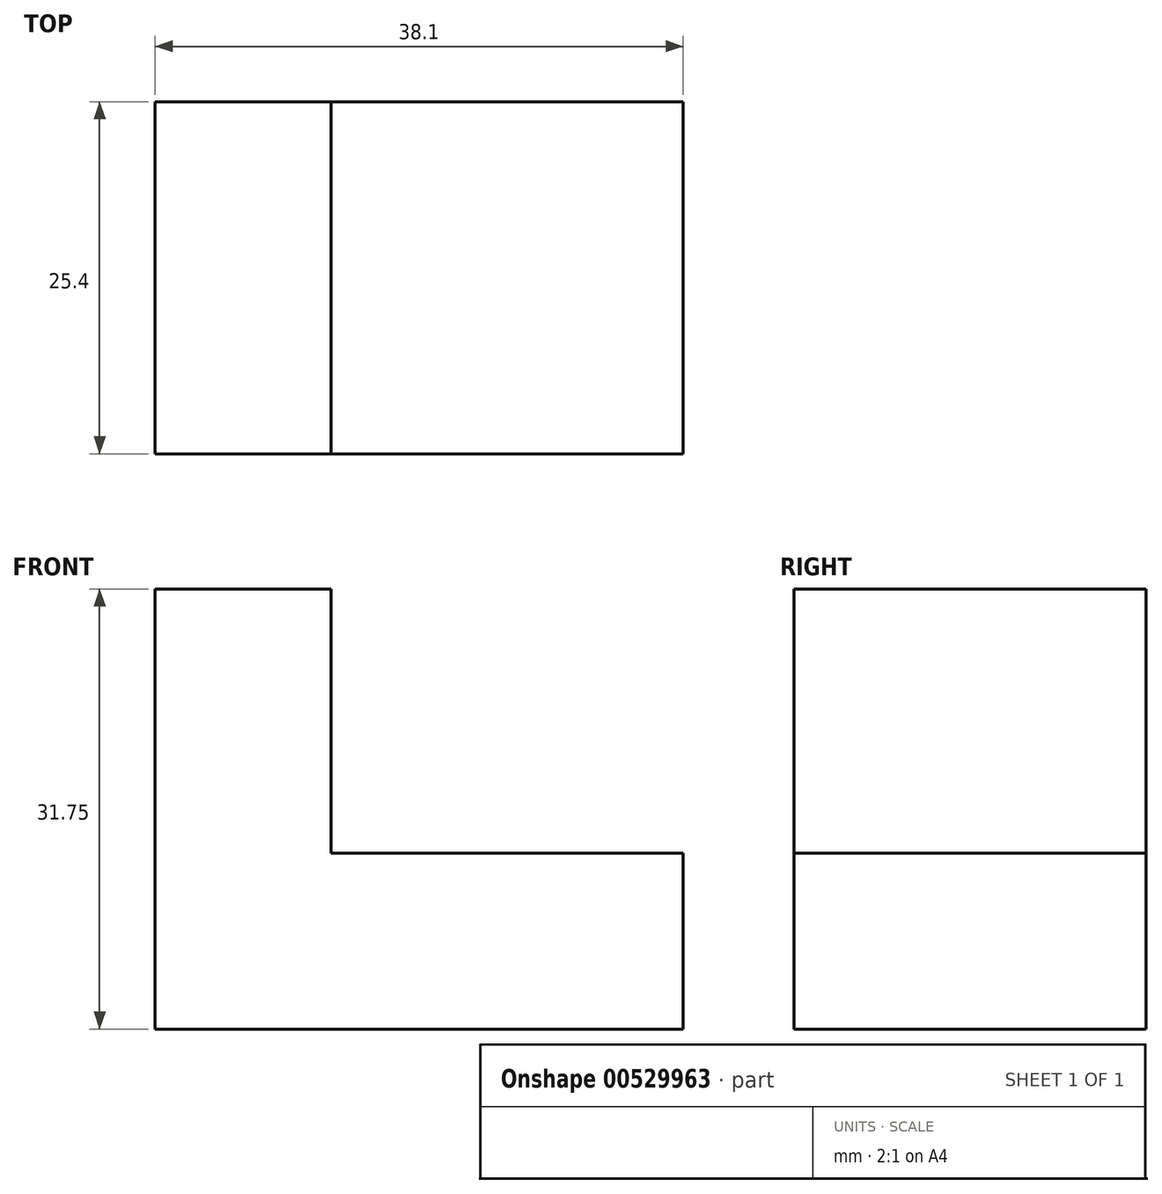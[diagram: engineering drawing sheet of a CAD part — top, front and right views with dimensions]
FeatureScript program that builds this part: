
annotation { "Feature Type Name" : "Feature", "Feature Type Description" : "" }
export const myFeature = defineFeature(function(context is Context, id is Id, definition is map)
    precondition{}
    {
        {
            var Q0;
            Q0=qCreatedBy(makeId("Front.planeOp"),FACE);
            var sketch = newSketch(context, id + "F0", { "sketchPlane" : qUnion([Q0])});
            skLineSegment(sketch, "E0", {"start": v(-61.6, 46.13) * mm, "end": v(-48.9, 46.13) * mm});
            skLineSegment(sketch, "E1", {"start": v(-61.6, 46.13) * mm, "end": v(-61.6, 14.38) * mm});
            skLineSegment(sketch, "E2", {"start": v(-61.6, 14.38) * mm, "end": v(-23.5, 14.38) * mm});
            skLineSegment(sketch, "E3", {"start": v(-48.9, 46.13) * mm, "end": v(-48.9, 27.08) * mm});
            skLineSegment(sketch, "E4", {"start": v(-23.5, 14.38) * mm, "end": v(-23.5, 27.08) * mm});
            skLineSegment(sketch, "E5", {"start": v(-23.5, 27.08) * mm, "end": v(-48.9, 27.08) * mm});
            skSolve(sketch);
        }
        {
            var Q0;
            Q0 = qSketchRegion(id + "F0", true);
            extrude(context, id + "F1", {"entities" : qUnion([Q0]), "depth" : 25.4 * mm, "offsetDistance" : 25.4 * mm});
        }
    });
